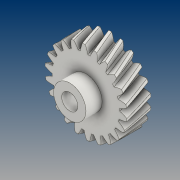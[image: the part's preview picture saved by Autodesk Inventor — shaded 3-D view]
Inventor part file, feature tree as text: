
AUTODESK INVENTOR PART (.ipt)
format: ipt  version: 2021 (Build 250183000, 183)  size: 480,256 bytes
history: native  units: mm (DEFAULTED — no unit token found)
features: extrude x3, plane x3, other x3, sketch x3
ambient origin geometry x8: Origin, YZ Plane, XZ Plane, XY Plane, X Axis, Y Axis, Z Axis, Center Point
bodies: Solid1 (feature_tree)
feature tree (12):
  extrude  "Extrusion1"  Depth=15.0mm TaperAngle=0.0deg
  plane  "Work Plane2"
  plane  "Work Plane8"
  plane  "Work Plane9"
  other  "Spur Gear"
  sketch  "Sketch3"  dims[d16=70.0mm d17=0.0mm d34=1.427997mm d39=0.0mm d41=0.0mm d43=70.0mm d46=70.0mm d47=0.0mm d48=0.0mm d49=10.0mm d50=5.0mm d51=0.0mm d52=0.0mm d53=10.0mm d54=0.0mm]
  extrude  "Extrusion2"  Depth=10.0mm TaperAngle=0.0deg
  extrude  "Extrusion3"  Depth=10.0mm TaperAngle=0.0deg
  sketch  "Sketch1"  dims[d0=50.766383mm d1=15.0mm d2=0.0mm]
  sketch  "Sketch2"  dims[d3=46.823822mm d4=10.0mm d5=0.0mm]
  other  "Srf1"
  other  "Pitch Diameter"
